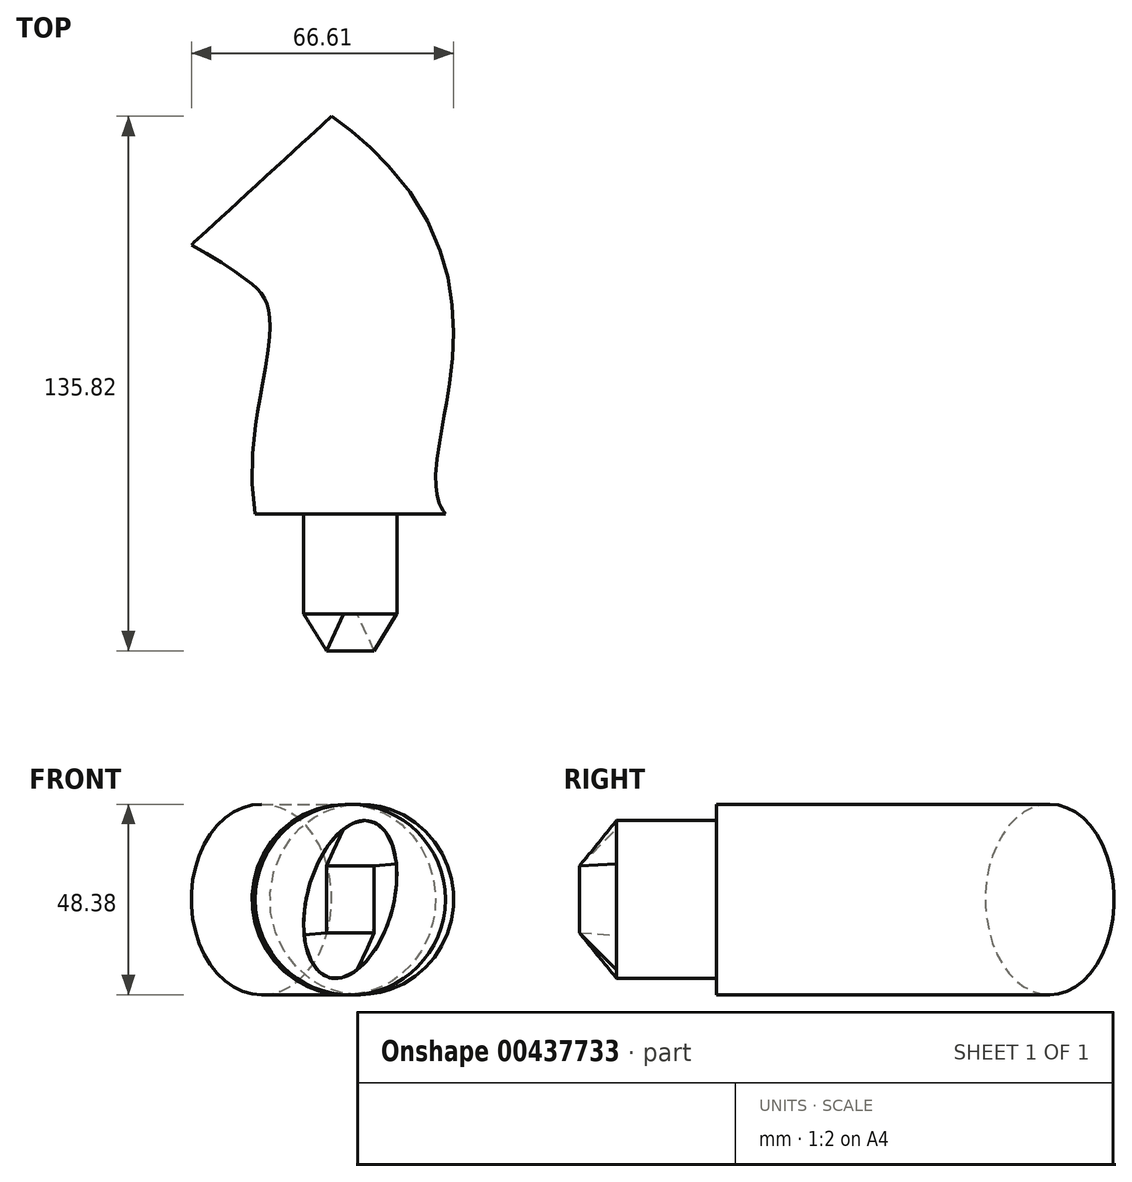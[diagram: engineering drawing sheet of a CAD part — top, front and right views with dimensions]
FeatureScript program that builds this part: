
annotation { "Feature Type Name" : "Feature", "Feature Type Description" : "" }
export const myFeature = defineFeature(function(context is Context, id is Id, definition is map)
    precondition{}
    {
        {
            var Q0;
            Q0=qCreatedBy(makeId("Front.planeOp"),FACE);
            var sketch = newSketch(context, id + "F0", { "sketchPlane" : qUnion([Q0])});
            skCircle(sketch, "E0", {"center": v(0, 0) * mm, "radius": 24.19 * mm});
            skSolve(sketch);
        }
        {
            var Q0;
            Q0=qCreatedBy(makeId("Top.planeOp"),FACE);
            var sketch = newSketch(context, id + "F1", { "sketchPlane" : qUnion([Q0])});
            skFitSpline(sketch, "E1", {"points": [v(0, 0) * mm, v(-22.55, 84.67) * mm], "startDerivative": vector(-22.55, 84.67) * mm, "endDerivative": vector(-132.53, 84.67) * mm});
            skSolve(sketch);
        }
        {
            var Q0;
            Q0=makeQuery(id+"F0.imprint","IMPRINT",FACE,{"disambiguationData":[TD([[makeQuery(id+"F0.imprint","IMPRINT",EDGE,{"derivedFrom":sQuery(id+"F0.wireOp",EDGE,"E0")}),1.0]])]});
            var Q1;
            Q1=sQuery(id+"F1.wireOp",EDGE,"E1");
            sweep(context, id + "F2", {"profiles" : qUnion([Q0]), "path" : qUnion([Q1])});
        }
        {
            var Q0;
            Q0=qCreatedBy(makeId("Front.planeOp"),FACE);
            var sketch = newSketch(context, id + "F3", { "sketchPlane" : qUnion([Q0])});
            skEllipse(sketch, "E2", {"center": v(0, 0) * mm, "majorRadius": 20.55 * mm, "minorRadius": 10.96 * mm, "majorAxis": v(-0.26, -0.97)});
            skSolve(sketch);
        }
        {
            var Q0;
            Q0=makeQuery(id+"F3.imprint","IMPRINT",FACE,{"disambiguationData":[TD([[makeQuery(id+"F3.imprint","IMPRINT",EDGE,{"derivedFrom":sQuery(id+"F3.wireOp",EDGE,"E2")}),1.0]])]});
            extrude(context, id + "F4", {"entities" : qUnion([Q0]), "operationType" : NewBodyOperationType.ADD, "depth" : 25.4 * mm, "hasSecondDirection" : true, "secondDirectionOppositeDirection" : true, "secondDirectionDepth" : 25.4 * mm});
        }
        {
            var Q0;
            Q0=qCreatedBy(makeId("Front.planeOp"),FACE);
            cPlane(context, id + "F5", {"entities" : qUnion([Q0]), "cplaneType" : CPlaneType.OFFSET, "offset" : 34.8 * mm, "width" : 152.4 * mm, "height" : 152.4 * mm});
        }
        {
            var Q0;
            Q0=qCreatedBy(id+"F5.planeOp",FACE);
            var sketch = newSketch(context, id + "F6", { "sketchPlane" : qUnion([Q0])});
            skLineSegment(sketch, "E3.bottom", {"start": v(-6.1, -8.5) * mm, "end": v(6.1, -8.5) * mm});
            skLineSegment(sketch, "E3.top", {"start": v(-6.1, 8.5) * mm, "end": v(6.1, 8.5) * mm});
            skLineSegment(sketch, "E3.left", {"start": v(-6.1, -8.5) * mm, "end": v(-6.1, 8.5) * mm});
            skLineSegment(sketch, "E3.right", {"start": v(6.1, -8.5) * mm, "end": v(6.1, 8.5) * mm});
            skPoint(sketch, "E3.middle", {"position": v(0, 0) * mm});
            skSolve(sketch);
        }
        {
            var Q0;
            Q0 = qSketchRegion(id + "F6", true);
            var Q1;
            Q1=makeQuery(id+"F4.opExtrude","CAP_FACE",FACE,{"disambiguationData":[OSD([sQuery(id+"F3.wireOp",EDGE,"E2")])],"isStart":false});
            loft(context, id + "F7", {"sheetProfilesArray" : [{ "sheetProfileEntities" : qUnion([Q0]) }, { "sheetProfileEntities" : qUnion([Q1]) }]});
        }
    });
